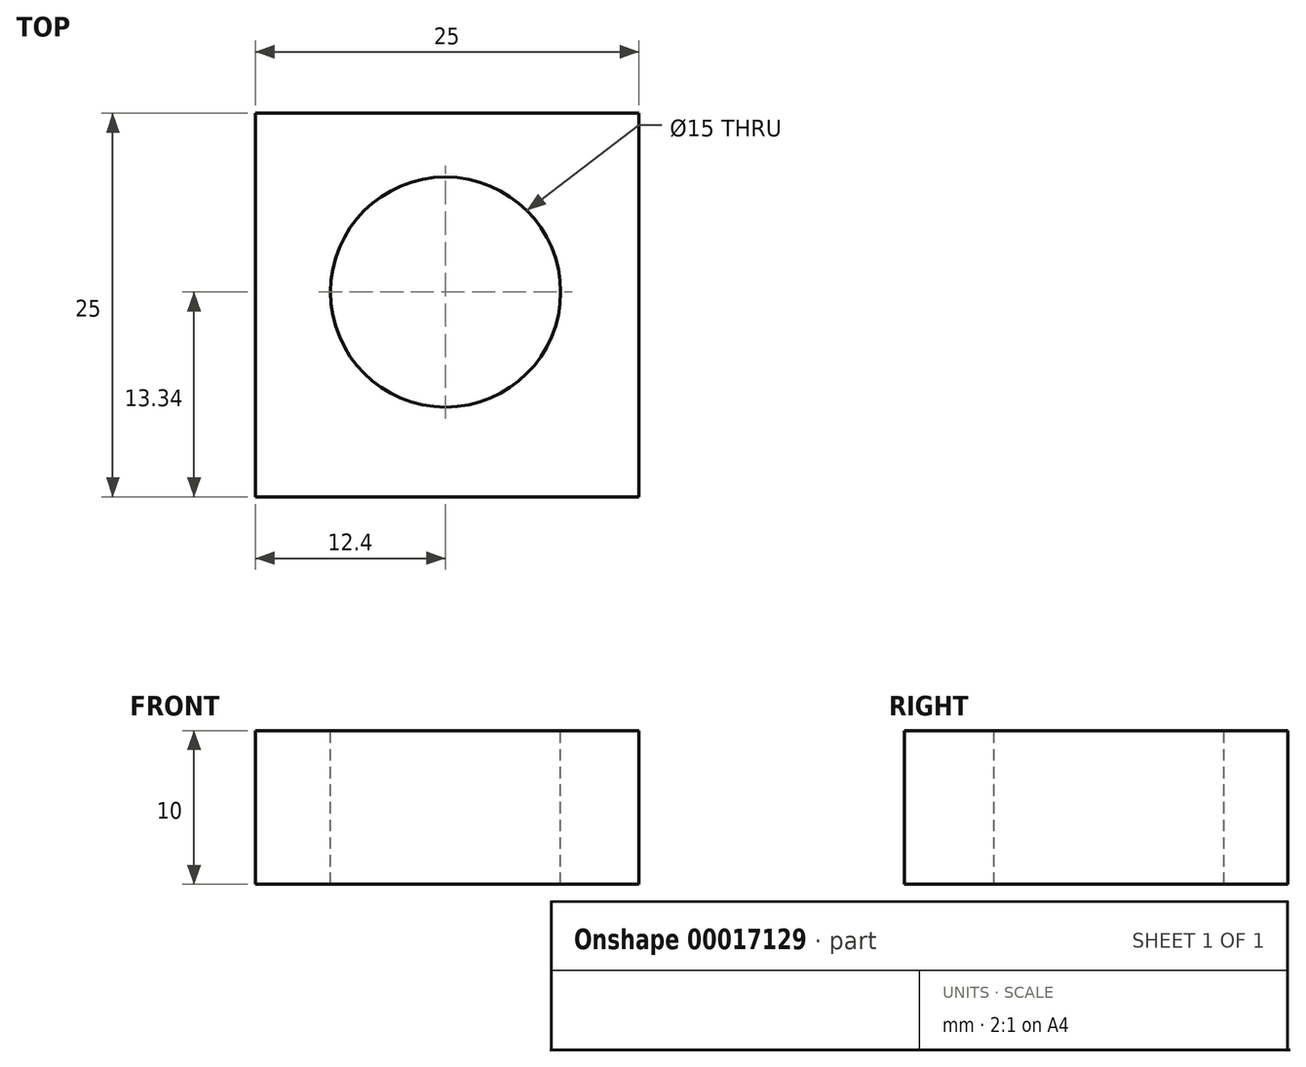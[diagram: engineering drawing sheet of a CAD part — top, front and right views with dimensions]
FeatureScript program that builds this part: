
annotation { "Feature Type Name" : "Feature", "Feature Type Description" : "" }
export const myFeature = defineFeature(function(context is Context, id is Id, definition is map)
    precondition{}
    {
        {
            var Q0;
            Q0=qCreatedBy(makeId("Front.planeOp"),FACE);
            var sketch = newSketch(context, id + "F0", { "sketchPlane" : qUnion([Q0])});
            skLineSegment(sketch, "E0.bottom", {"start": v(-12.4, 0) * mm, "end": v(12.6, 0) * mm});
            skLineSegment(sketch, "E0.top", {"start": v(-12.4, 10) * mm, "end": v(12.6, 10) * mm});
            skLineSegment(sketch, "E0.left", {"start": v(-12.4, 0) * mm, "end": v(-12.4, 10) * mm});
            skLineSegment(sketch, "E0.right", {"start": v(12.6, 0) * mm, "end": v(12.6, 10) * mm});
            skSolve(sketch);
        }
        {
            var Q0;
            Q0 = qSketchRegion(id + "F0", true);
            extrude(context, id + "F1", {"entities" : qUnion([Q0]), "depth" : 25 * mm});
        }
        {
            var Q0;
            Q0=makeQuery(id+"F1.opExtrude","SWEPT_FACE",FACE,{"disambiguationData":[OSD([sQuery(id+"F0.wireOp",EDGE,"E0.top")])]});
            var sketch = newSketch(context, id + "F2", { "sketchPlane" : qUnion([Q0])});
            skCircle(sketch, "E1", {"center": v(0, -11.66) * mm, "radius": 7.5 * mm});
            skSolve(sketch);
        }
        {
            var Q0;
            Q0=sQuery(id+"F2.wireOp",VERTEX,"E1.center");
            var Q1;
            Q1=makeQuery(id+"F1.opExtrude","SWEPT_BODY",BODY,{"disambiguationData":[OSD([sQuery(id+"F0.wireOp",EDGE,"E0.bottom"),sQuery(id+"F0.wireOp",EDGE,"E0.top"),sQuery(id+"F0.wireOp",EDGE,"E0.left"),sQuery(id+"F0.wireOp",EDGE,"E0.right")])]});
            hole(context, id + "F3", {"style" : HoleStyle.SIMPLE, "holeDiameter" : 15 * mm, "endStyle" : HoleEndStyle.THROUGH, "locations" : qUnion([Q0]), "scope" : qUnion([Q1])});
        }
    });
